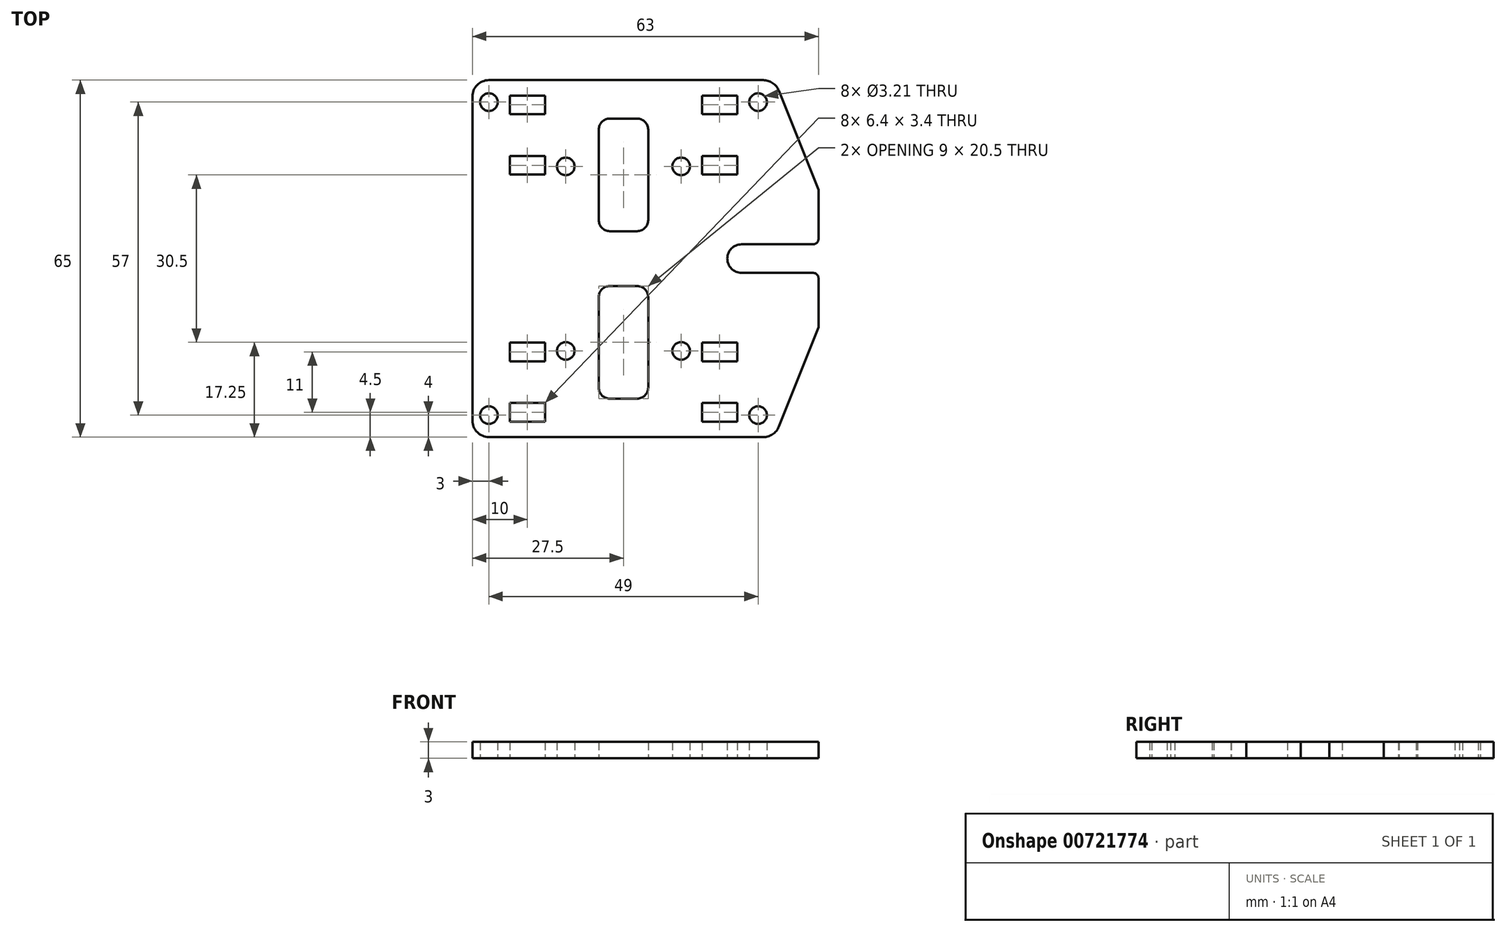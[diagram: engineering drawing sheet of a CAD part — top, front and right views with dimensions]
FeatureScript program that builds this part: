
annotation { "Feature Type Name" : "Feature", "Feature Type Description" : "" }
export const myFeature = defineFeature(function(context is Context, id is Id, definition is map)
    precondition{}
    {
        {
            var Q0;
            Q0=qCreatedBy(makeId("Top.planeOp"),FACE);
            var sketch = newSketch(context, id + "F0", { "sketchPlane" : qUnion([Q0])});
            skArc(sketch, "E0", {"start": v(0.5, 23.5) * mm, "mid": v(-0.09, 24.91) * mm, "end": v(-1.5, 25.5) * mm});
            skLineSegment(sketch, "E1", {"start": v(-6.5, 25.5) * mm, "end": v(-1.5, 25.5) * mm});
            skArc(sketch, "E2", {"start": v(-6.5, 25.5) * mm, "mid": v(-7.91, 24.91) * mm, "end": v(-8.5, 23.5) * mm});
            skArc(sketch, "E3", {"start": v(-1.5, -25.5) * mm, "mid": v(-0.09, -24.91) * mm, "end": v(0.5, -23.5) * mm});
            skLineSegment(sketch, "E4", {"start": v(-1.5, -25.5) * mm, "end": v(-6.5, -25.5) * mm});
            skArc(sketch, "E5", {"start": v(-8.5, -23.5) * mm, "mid": v(-7.91, -24.91) * mm, "end": v(-6.5, -25.5) * mm});
            skLineSegment(sketch, "E6", {"start": v(-8.5, 7) * mm, "end": v(-8.5, 23.5) * mm});
            skArc(sketch, "E7", {"start": v(-8.5, 7) * mm, "mid": v(-7.91, 5.59) * mm, "end": v(-6.5, 5) * mm});
            skLineSegment(sketch, "E8", {"start": v(0.5, 23.5) * mm, "end": v(0.5, 7) * mm});
            skLineSegment(sketch, "E9", {"start": v(-6.5, 5) * mm, "end": v(-1.5, 5) * mm});
            skArc(sketch, "E10", {"start": v(-1.5, 5) * mm, "mid": v(-0.09, 5.59) * mm, "end": v(0.5, 7) * mm});
            skLineSegment(sketch, "E11", {"start": v(-8.5, -23.5) * mm, "end": v(-8.5, -7) * mm});
            skArc(sketch, "E12", {"start": v(-6.5, -5) * mm, "mid": v(-7.91, -5.59) * mm, "end": v(-8.5, -7) * mm});
            skLineSegment(sketch, "E13", {"start": v(-6.5, -5) * mm, "end": v(-1.5, -5) * mm});
            skLineSegment(sketch, "E14", {"start": v(0.5, -7) * mm, "end": v(0.5, -23.5) * mm});
            skArc(sketch, "E15", {"start": v(0.5, -7) * mm, "mid": v(-0.09, -5.59) * mm, "end": v(-1.5, -5) * mm});
            skCircle(sketch, "E16", {"center": v(-14.5, 16.8) * mm, "radius": 1.6 * mm});
            skCircle(sketch, "E17", {"center": v(-28.5, -28.5) * mm, "radius": 1.6 * mm});
            skCircle(sketch, "E18", {"center": v(-28.5, 28.5) * mm, "radius": 1.6 * mm});
            skLineSegment(sketch, "E19", {"start": v(-18.3, 26.3) * mm, "end": v(-18.3, 29.7) * mm});
            skLineSegment(sketch, "E20", {"start": v(-18.3, 29.7) * mm, "end": v(-24.7, 29.7) * mm});
            skLineSegment(sketch, "E21", {"start": v(-18.3, 26.3) * mm, "end": v(-24.7, 26.3) * mm});
            skLineSegment(sketch, "E22", {"start": v(-24.7, 29.7) * mm, "end": v(-24.7, 26.3) * mm});
            skLineSegment(sketch, "E23", {"start": v(-18.3, 15.3) * mm, "end": v(-18.3, 18.7) * mm});
            skLineSegment(sketch, "E24", {"start": v(-18.3, 18.7) * mm, "end": v(-24.7, 18.7) * mm});
            skLineSegment(sketch, "E25", {"start": v(-18.3, 15.3) * mm, "end": v(-24.7, 15.3) * mm});
            skLineSegment(sketch, "E26", {"start": v(-24.7, 18.7) * mm, "end": v(-24.7, 15.3) * mm});
            skLineSegment(sketch, "E27", {"start": v(-18.3, -18.7) * mm, "end": v(-18.3, -15.3) * mm});
            skLineSegment(sketch, "E28", {"start": v(-18.3, -15.3) * mm, "end": v(-24.7, -15.3) * mm});
            skLineSegment(sketch, "E29", {"start": v(-18.3, -18.7) * mm, "end": v(-24.7, -18.7) * mm});
            skLineSegment(sketch, "E30", {"start": v(-24.7, -15.3) * mm, "end": v(-24.7, -18.7) * mm});
            skLineSegment(sketch, "E31", {"start": v(-18.3, -29.7) * mm, "end": v(-18.3, -26.3) * mm});
            skLineSegment(sketch, "E32", {"start": v(-18.3, -26.3) * mm, "end": v(-24.7, -26.3) * mm});
            skLineSegment(sketch, "E33", {"start": v(-18.3, -29.7) * mm, "end": v(-24.7, -29.7) * mm});
            skLineSegment(sketch, "E34", {"start": v(-24.7, -26.3) * mm, "end": v(-24.7, -29.7) * mm});
            skCircle(sketch, "E35", {"center": v(20.5, 28.5) * mm, "radius": 1.6 * mm});
            skCircle(sketch, "E36", {"center": v(6.5, 16.8) * mm, "radius": 1.6 * mm});
            skCircle(sketch, "E37", {"center": v(20.5, -28.5) * mm, "radius": 1.6 * mm});
            skLineSegment(sketch, "E38", {"start": v(16.7, 26.3) * mm, "end": v(16.7, 29.7) * mm});
            skLineSegment(sketch, "E39", {"start": v(16.7, 29.7) * mm, "end": v(10.3, 29.7) * mm});
            skLineSegment(sketch, "E40", {"start": v(16.7, 26.3) * mm, "end": v(10.3, 26.3) * mm});
            skLineSegment(sketch, "E41", {"start": v(10.3, 29.7) * mm, "end": v(10.3, 26.3) * mm});
            skLineSegment(sketch, "E42", {"start": v(16.7, 15.3) * mm, "end": v(16.7, 18.7) * mm});
            skLineSegment(sketch, "E43", {"start": v(16.7, 18.7) * mm, "end": v(10.3, 18.7) * mm});
            skLineSegment(sketch, "E44", {"start": v(16.7, 15.3) * mm, "end": v(10.3, 15.3) * mm});
            skLineSegment(sketch, "E45", {"start": v(10.3, 18.7) * mm, "end": v(10.3, 15.3) * mm});
            skLineSegment(sketch, "E46", {"start": v(16.7, -18.7) * mm, "end": v(16.7, -15.3) * mm});
            skLineSegment(sketch, "E47", {"start": v(16.7, -15.3) * mm, "end": v(10.3, -15.3) * mm});
            skLineSegment(sketch, "E48", {"start": v(16.7, -18.7) * mm, "end": v(10.3, -18.7) * mm});
            skLineSegment(sketch, "E49", {"start": v(10.3, -15.3) * mm, "end": v(10.3, -18.7) * mm});
            skLineSegment(sketch, "E50", {"start": v(16.7, -29.7) * mm, "end": v(16.7, -26.3) * mm});
            skLineSegment(sketch, "E51", {"start": v(16.7, -26.3) * mm, "end": v(10.3, -26.3) * mm});
            skLineSegment(sketch, "E52", {"start": v(16.7, -29.7) * mm, "end": v(10.3, -29.7) * mm});
            skLineSegment(sketch, "E53", {"start": v(10.3, -26.3) * mm, "end": v(10.3, -29.7) * mm});
            skCircle(sketch, "E54", {"center": v(-14.5, -16.8) * mm, "radius": 1.6 * mm});
            skCircle(sketch, "E55", {"center": v(6.5, -16.8) * mm, "radius": 1.6 * mm});
            skArc(sketch, "E56", {"start": v(17.5, 2.6) * mm, "mid": v(14.9, 0) * mm, "end": v(17.5, -2.6) * mm});
            skLineSegment(sketch, "E57", {"start": v(31.5, 12.5) * mm, "end": v(31.5, 3.6) * mm});
            skLineSegment(sketch, "E58", {"start": v(17.5, 2.6) * mm, "end": v(30.5, 2.6) * mm});
            skArc(sketch, "E59", {"start": v(30.5, 2.6) * mm, "mid": v(31.2, 2.9) * mm, "end": v(31.5, 3.6) * mm});
            skLineSegment(sketch, "E60", {"start": v(17.5, -2.6) * mm, "end": v(30.5, -2.6) * mm});
            skLineSegment(sketch, "E61", {"start": v(31.5, -12.5) * mm, "end": v(31.5, -3.6) * mm});
            skArc(sketch, "E62", {"start": v(31.5, -3.6) * mm, "mid": v(31.2, -2.9) * mm, "end": v(30.5, -2.6) * mm});
            skArc(sketch, "E63", {"start": v(24.25, 30.61) * mm, "mid": v(23.15, 31.98) * mm, "end": v(21.47, 32.5) * mm});
            skLineSegment(sketch, "E64", {"start": v(31.5, -12.5) * mm, "end": v(24.25, -30.61) * mm});
            skArc(sketch, "E65", {"start": v(21.47, -32.5) * mm, "mid": v(23.15, -31.98) * mm, "end": v(24.25, -30.61) * mm});
            skLineSegment(sketch, "E66", {"start": v(21.47, -32.5) * mm, "end": v(-28.5, -32.5) * mm});
            skArc(sketch, "E67", {"start": v(-31.5, -29.5) * mm, "mid": v(-30.62, -31.62) * mm, "end": v(-28.5, -32.5) * mm});
            skLineSegment(sketch, "E68", {"start": v(21.47, 32.5) * mm, "end": v(-28.5, 32.5) * mm});
            skArc(sketch, "E69", {"start": v(-28.5, 32.5) * mm, "mid": v(-30.62, 31.62) * mm, "end": v(-31.5, 29.5) * mm});
            skLineSegment(sketch, "E70", {"start": v(24.25, 30.61) * mm, "end": v(31.5, 12.5) * mm});
            skLineSegment(sketch, "E71", {"start": v(-31.5, 29.5) * mm, "end": v(-31.5, -29.5) * mm});
            skSolve(sketch);
        }
        {
            var Q0;
            Q0=qSketchRegion(id+"F0",true);
            extrude(context, id + "F1", {"entities" : qUnion([Q0]), "depth" : 3 * mm, "offsetDistance" : 25 * mm});
        }
    });
